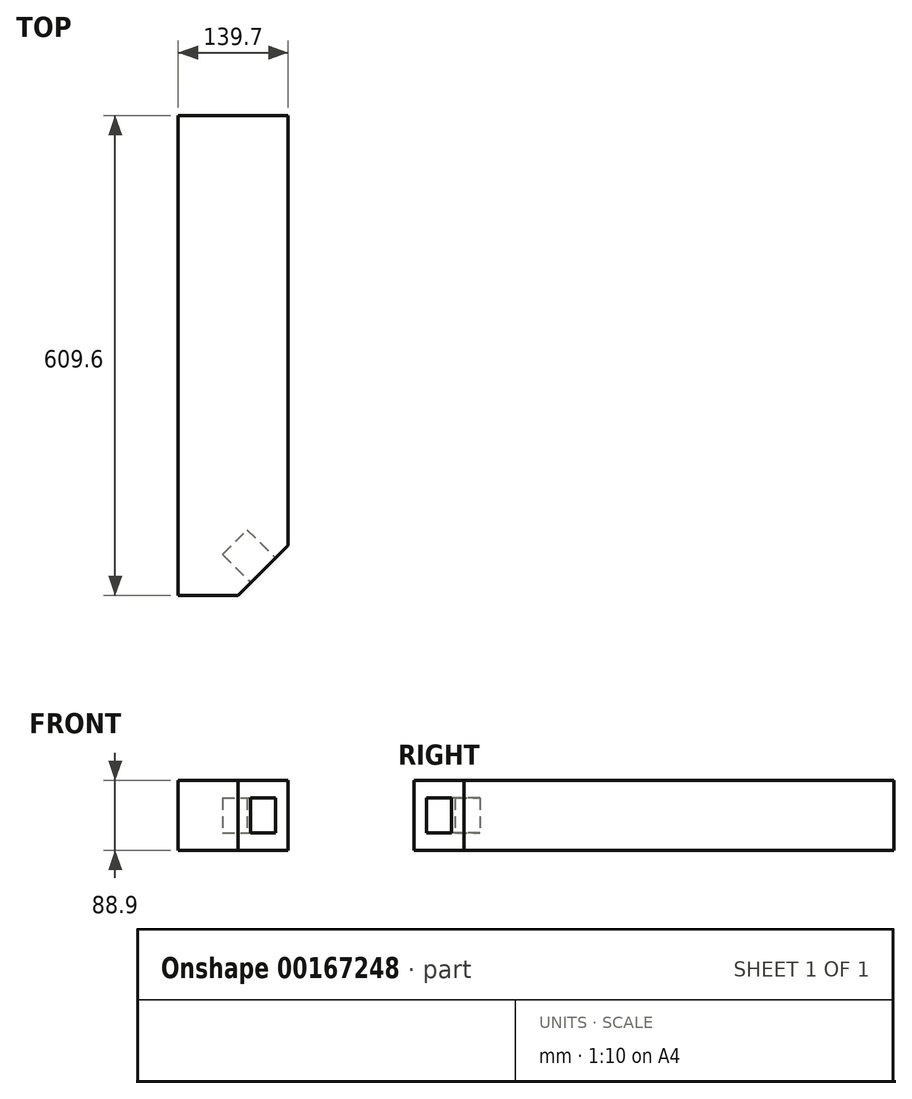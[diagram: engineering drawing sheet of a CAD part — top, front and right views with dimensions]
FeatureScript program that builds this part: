
annotation { "Feature Type Name" : "Feature", "Feature Type Description" : "" }
export const myFeature = defineFeature(function(context is Context, id is Id, definition is map)
    precondition{}
    {
        {
            var Q0;
            Q0=qCreatedBy(makeId("Front.planeOp"),FACE);
            var sketch = newSketch(context, id + "F0", { "sketchPlane" : qUnion([Q0])});
            skLineSegment(sketch, "E0.bottom", {"start": v(0, 0) * mm, "end": v(139.7, 0) * mm});
            skLineSegment(sketch, "E0.top", {"start": v(0, 88.9) * mm, "end": v(139.7, 88.9) * mm});
            skLineSegment(sketch, "E0.left", {"start": v(0, 0) * mm, "end": v(0, 88.9) * mm});
            skLineSegment(sketch, "E0.right", {"start": v(139.7, 0) * mm, "end": v(139.7, 88.9) * mm});
            skSolve(sketch);
        }
        {
            var Q0;
            Q0=makeQuery(id+"F0.imprint","IMPRINT",FACE,{"disambiguationData":[TD([[makeQuery(id+"F0.imprint","IMPRINT",EDGE,{"derivedFrom":sQuery(id+"F0.wireOp",EDGE,"E0.bottom")}),1.0]])]});
            extrude(context, id + "F1", {"entities" : qUnion([Q0]), "depth" : 609.6 * mm});
        }
        {
            var Q0;
            Q0=makeQuery(id+"F1.opExtrude","CAP_EDGE",EDGE,{"disambiguationData":[OSD([sQuery(id+"F0.wireOp",EDGE,"E0.right")])],"isStart":false});
            chamfer(context, id + "F2", {"entities" : qUnion([Q0]), "width" : 63.5 * mm, "tangentPropagation" : true});
        }
        {
            var Q0;
            Q0=makeQuery(id+"F2.opChamfer","BLEND_FACE",FACE,{"disambiguationData":[OSD([sQuery(id+"F0.wireOp",EDGE,"E0.right")])]});
            var sketch = newSketch(context, id + "F3", { "sketchPlane" : qUnion([Q0])});
            skLineSegment(sketch, "E1", {"start": v(-377.17, 88.9) * mm, "end": v(-287.37, 0) * mm, "construction": true});
            skLineSegment(sketch, "E2", {"start": v(-287.37, 88.9) * mm, "end": v(-377.17, 0) * mm, "construction": true});
            skPoint(sketch, "E3.middle", {"position": v(-332.27, 44.45) * mm});
            skLineSegment(sketch, "E4.bottom", {"start": v(-354.5, 66.45) * mm, "end": v(-310.04, 66.45) * mm});
            skLineSegment(sketch, "E4.top", {"start": v(-354.5, 22.45) * mm, "end": v(-310.04, 22.45) * mm});
            skLineSegment(sketch, "E4.left", {"start": v(-354.5, 66.45) * mm, "end": v(-354.5, 22.45) * mm});
            skLineSegment(sketch, "E4.right", {"start": v(-310.04, 66.45) * mm, "end": v(-310.04, 22.45) * mm});
            skSolve(sketch);
        }
        {
            var Q0;
            Q0=makeQuery(id+"F3.imprint","IMPRINT",FACE,{"disambiguationData":[TD([[makeQuery(id+"F3.imprint","IMPRINT",EDGE,{"derivedFrom":sQuery(id+"F3.wireOp",EDGE,"E4.bottom")}),-1.0]])]});
            extrude(context, id + "F4", {"entities" : qUnion([Q0]), "operationType" : NewBodyOperationType.REMOVE, "oppositeDirection" : true, "depth" : 50.8 * mm});
        }
    });
